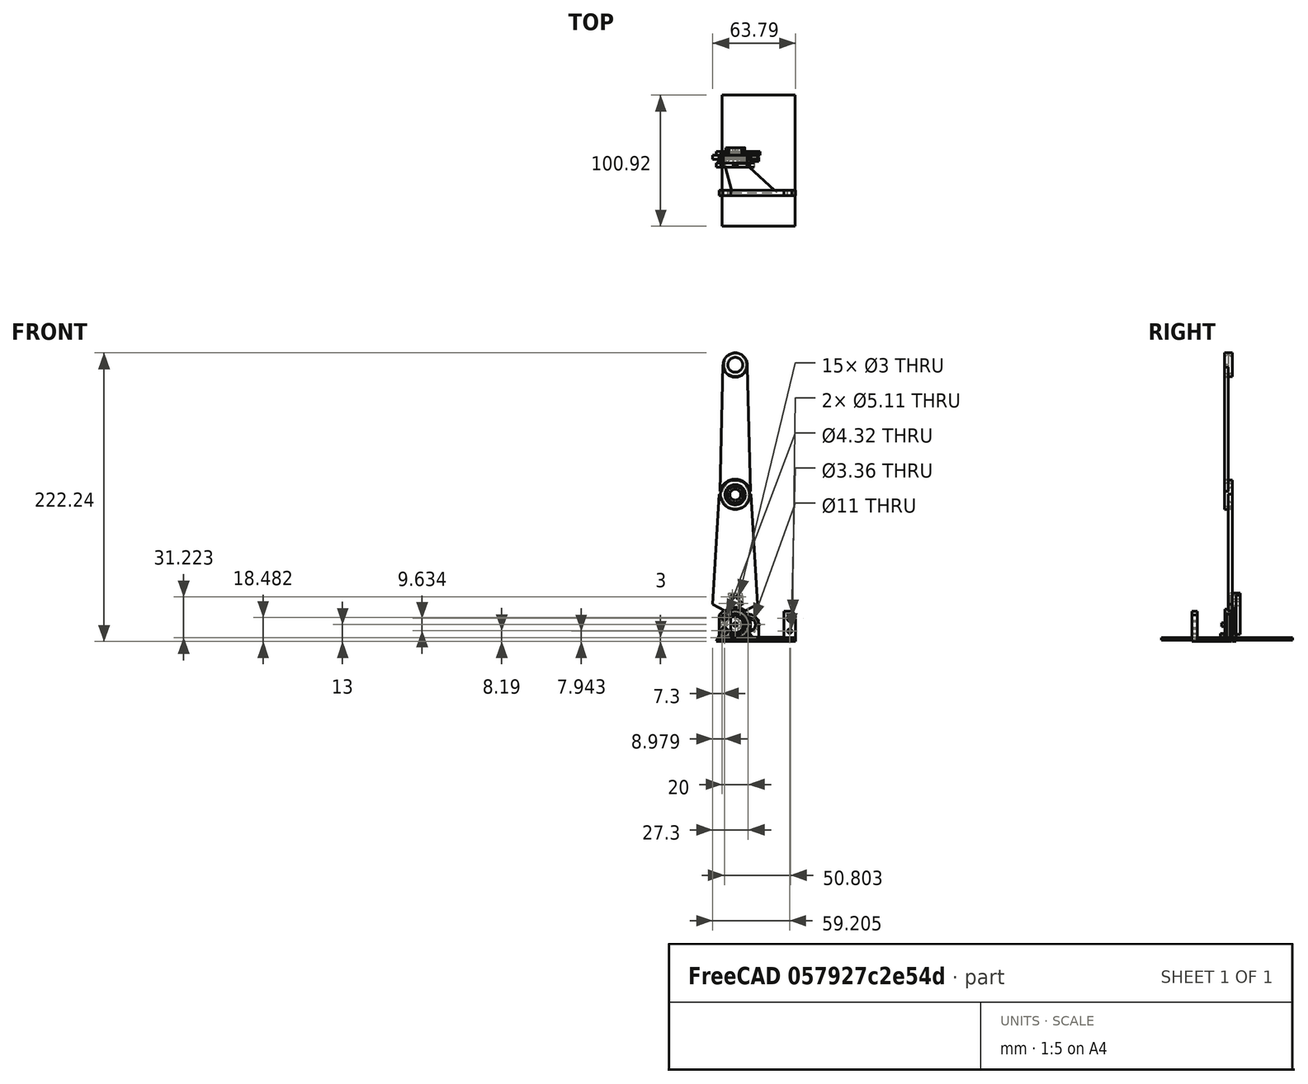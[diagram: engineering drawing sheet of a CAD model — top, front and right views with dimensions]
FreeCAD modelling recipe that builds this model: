
FCSTD DOCUMENT  (FreeCAD 0.16RUnknown)
Label: Arm
License: CreativeCommons Attribution-NonCommercial
LicenseURL: http://creativecommons.org/licenses/by-nc/4.0/
objects: Sketcher::SketchObject×25, PartDesign::Pad×12, PartDesign::Revolution×6, Mesh::Feature×3, Part::Cut×3, Part::Cylinder×2, Part::MultiFuse×2, Part::FeaturePython×2
note: 70 computed .brp shape members not serialized (recipe doc carries the construction recipe); baked Part::Feature solids carry a one-line shape summary decoded from their .brp

FEATURE [Mesh::Feature] ParallaxServo
  Placement = pos=(2,50,0) rot=(1,0,0;1.5708rad)
FEATURE [Sketcher::SketchObject] Sketch
  sketch-geometry (1):
    g0: Circle CenterX=0 CenterY=0 CenterZ=0 NormalX=0 NormalY=0 NormalZ=1 Radius=85.2865
  constraints (1):
    c: Coincident(g0,g-1)
FEATURE [Mesh::Feature] ParallaxServo001
  Placement = pos=(15,-50,0) rot=(0.57735,-0.57735,-0.57735;4.18879rad)
FEATURE [Sketcher::SketchObject] Sketch001
  Placement = pos=(10,0,0) rot=(1,0,0;1.5708rad)
  sketch-geometry (6):
    g0: Circle CenterX=0 CenterY=0 CenterZ=0 NormalX=0 NormalY=0 NormalZ=1 Radius=5.5
    g1: ArcOfCircle CenterX=0 CenterY=0 CenterZ=0 NormalX=0 NormalY=0 NormalZ=1 Radius=8 StartAngle=0 EndAngle=3.14159
    g2: LineSegment StartX=-8 StartY=0 StartZ=0 EndX=-8 EndY=-10 EndZ=0
    g3: LineSegment StartX=-8 StartY=-10 StartZ=0 EndX=8 EndY=-10 EndZ=0
    g4: LineSegment StartX=8 StartY=-10 StartZ=0 EndX=8 EndY=0 EndZ=0
    g5: LineSegment [constr] StartX=-8 StartY=0 StartZ=0 EndX=-5.5 EndY=0 EndZ=0
  constraints (17):
    c: PointOnObject(g0,g-1)
    c: Coincident(g0,g-1)
    c: Radius(g0) = 5.5
    c: Coincident(g1,g-1)
    c: PointOnObject(g1,g-1)
    c: PointOnObject(g1,g-1)
    c: Tangent(g1,g2) = -1.5708
    c: Coincident(g2,g3)
    c: Horizontal(g3)
    c: Coincident(g3,g4)
    c: Coincident(g4,g1)
    c: Vertical(g4)
    c: DistanceY(g2,g-1) = 10
    c: Coincident(g5,g1)
    c: PointOnObject(g5,g0)
    c: Horizontal(g5)
    c: DistanceX(g5,g5) = 2.5
FEATURE [Sketcher::SketchObject] Sketch002
  Placement = pos=(0,0,-10) rot=(0,0,1;0rad)
  sketch-geometry (4):
    g0: LineSegment StartX=-10.0536 StartY=49.3948 StartZ=0 EndX=45.9875 EndY=49.3948 EndZ=0
    g1: LineSegment StartX=45.9875 StartY=49.3948 StartZ=0 EndX=45.9875 EndY=-51.5305 EndZ=0
    g2: LineSegment StartX=45.9875 StartY=-51.5305 StartZ=0 EndX=-10.0536 EndY=-51.5305 EndZ=0
    g3: LineSegment StartX=-10.0536 StartY=-51.5305 StartZ=0 EndX=-10.0536 EndY=49.3948 EndZ=0
  constraints (8):
    c: Coincident(g0,g1)
    c: Coincident(g1,g2)
    c: Coincident(g2,g3)
    c: Coincident(g3,g0)
    c: Horizontal(g0)
    c: Horizontal(g2)
    c: Vertical(g1)
    c: Vertical(g3)
FEATURE [PartDesign::Pad] Pad
  Length = 2
  Length2 = 100
  Placement = pos=(0,0,-10) rot=(0,0,1;0rad)
  Reversed = true
  Sketch = -> Sketch002
  Type = 0
FEATURE [PartDesign::Pad] Pad001
  Length = 3
  Length2 = 100
  Midplane = true
  Placement = pos=(10,0,0) rot=(1,0,0;1.5708rad)
  Sketch = -> Sketch001
  Type = 0
FEATURE [Sketcher::SketchObject] Sketch003
  Placement = pos=(0,0,0) rot=(-1,0,0;4.71239rad)
FEATURE [Sketcher::SketchObject] Sketch004
  Placement = pos=(0,0,0) rot=(0.57735,0.57735,0.57735;2.0944rad)
  sketch-geometry (13):
    g0: LineSegment [constr] StartX=-2.5 StartY=6.31119 StartZ=0 EndX=0 EndY=4.21345 EndZ=0
    g1: LineSegment StartX=0 StartY=4.21345 StartZ=0 EndX=2.5 EndY=6.31119 EndZ=0
    g2: LineSegment StartX=2.5 StartY=6.31119 StartZ=0 EndX=2.5 EndY=0 EndZ=0
    g3: LineSegment [constr] StartX=-2.5 StartY=0 StartZ=0 EndX=-2.5 EndY=6.31119 EndZ=0
    g4: LineSegment [constr] StartX=-2.5 StartY=6.31119 StartZ=0 EndX=2.5 EndY=6.31119 EndZ=0
    g5: Circle [constr] CenterX=0 CenterY=7.28115 CenterZ=0 NormalX=0 NormalY=0 NormalZ=1 Radius=2.35
    g6: LineSegment [constr] StartX=-2.5 StartY=0 StartZ=0 EndX=2.5 EndY=0 EndZ=0
    g7: Circle [constr] CenterX=-4.27975 CenterY=5.89058 CenterZ=0 NormalX=0 NormalY=0 NormalZ=1 Radius=2.25
    g8: Circle [constr] CenterX=0 CenterY=7.28115 CenterZ=0 NormalX=0 NormalY=0 NormalZ=1 Radius=2.25
    g9: ArcOfCircle [constr] CenterX=0 CenterY=0 CenterZ=0 NormalX=0 NormalY=0 NormalZ=1 Radius=7.28115 StartAngle=1.5708 EndAngle=2.19911
    g10: LineSegment [constr] StartX=-4.27975 StartY=5.89058 StartZ=0 EndX=0 EndY=0 EndZ=0
    g11: LineSegment StartX=0 StartY=4.21345 StartZ=0 EndX=0 EndY=0 EndZ=0
    g12: LineSegment StartX=0 StartY=0 StartZ=0 EndX=2.5 EndY=0 EndZ=0
  constraints (33):
    c: PointOnObject(g0,g-2)
    c: Coincident(g0,g1)
    c: Coincident(g1,g2)
    c: Coincident(g3,g0)
    c: Vertical(g3)
    c: Coincident(g4,g0)
    c: Coincident(g4,g1)
    c: Horizontal(g4)
    c: PointOnObject(g5,g-2)
    c: Tangent(g1,g5)
    c: Radius(g5) = 2.35
    c: Tangent(g5,g0)
    c: Angle(g1,g0) = 1.74533
    c: DistanceX(g4,g4) = 5
    c: Vertical(g2)
    c: Coincident(g6,g3)
    c: Coincident(g6,g2)
    c: PointOnObject(g3,g-1)
    c: PointOnObject(g2,g-1)
    c: Coincident(g8,g5)
    c: Radius(g8) = 2.25
    c: Equal(g8,g7)
    c: Tangent(g7,g8)
    c: Coincident(g9,g-1)
    c: Coincident(g9,g5)
    c: Coincident(g9,g7)
    c: Coincident(g10,g7)
    c: Coincident(g10,g-1)
    c: Angle(g-2,g10) = 0.628319
    c: Coincident(g0,g11)
    c: Coincident(g11,g12)
    c: Coincident(g12,g2)
    c: Coincident(g11,g-1)
FEATURE [PartDesign::Revolution] Revolution
  Angle = 360
  Axis = (0,1,0)
  Base = (0,0,0)
  Placement = pos=(0,0,0) rot=(0.57735,0.57735,0.57735;2.0944rad)
  ReferenceAxis = -> Sketch004 [H_Axis]
  Sketch = -> Sketch004
FEATURE [Sketcher::SketchObject] Sketch006
  Placement = pos=(0,0,0) rot=(1,0,0;1.5708rad)
  sketch-geometry (4):
    g0: Circle [constr] CenterX=0 CenterY=0 CenterZ=0 NormalX=0 NormalY=0 NormalZ=1 Radius=7.28115
    g1: Circle CenterX=7.28115 CenterY=0 CenterZ=0 NormalX=0 NormalY=0 NormalZ=1 Radius=2.25
    g2: Circle CenterX=5.89058 CenterY=4.27975 CenterZ=0 NormalX=0 NormalY=0 NormalZ=1 Radius=2.25
    g3: LineSegment [constr] StartX=5.89058 StartY=4.27975 StartZ=0 EndX=0 EndY=0 EndZ=0
  constraints (11):
    c: Coincident(g0,g-1)
    c: PointOnObject(g1,g0)
    c: PointOnObject(g2,g0)
    c: Equal(g2,g1)
    c: Coincident(g3,g2)
    c: Coincident(g3,g-1)
    c: Angle(g-1,g3) = 0.628319
    c: Tangent(g2,g1)
    c: Radius(g1) = 2.25
    c: PointOnObject(g1,g-1)
    c: Distance(g3) = 7.28115
FEATURE [Sketcher::SketchObject] Sketch007
  Placement = pos=(0,0,0) rot=(0.57735,0.57735,0.57735;2.0944rad)
  sketch-geometry (10):
    g0: Circle [constr] CenterX=0 CenterY=7.28115 CenterZ=0 NormalX=0 NormalY=0 NormalZ=1 Radius=2.35
    g1: Circle [constr] CenterX=-4.27975 CenterY=5.89058 CenterZ=0 NormalX=0 NormalY=0 NormalZ=1 Radius=2.25
    g2: Circle [constr] CenterX=0 CenterY=7.28115 CenterZ=0 NormalX=0 NormalY=0 NormalZ=1 Radius=2.25
    g3: ArcOfCircle [constr] CenterX=0 CenterY=0 CenterZ=0 NormalX=0 NormalY=0 NormalZ=1 Radius=7.28115 StartAngle=1.5708 EndAngle=2.19911
    g4: LineSegment [constr] StartX=-4.27975 StartY=5.89058 StartZ=0 EndX=0 EndY=0 EndZ=0
    g5: LineSegment StartX=-2.5 StartY=8.25111 StartZ=0 EndX=0 EndY=10.3489 EndZ=0
    g6: LineSegment StartX=0 StartY=10.3489 StartZ=0 EndX=2.5 EndY=8.25111 EndZ=0
    g7: LineSegment StartX=2.5 StartY=8.25111 StartZ=0 EndX=2.5 EndY=11.7511 EndZ=0
    g8: LineSegment StartX=2.5 StartY=11.7511 StartZ=0 EndX=-2.5 EndY=11.7511 EndZ=0
    g9: LineSegment StartX=-2.5 StartY=11.7511 StartZ=0 EndX=-2.5 EndY=8.25111 EndZ=0
  constraints (26):
    c: PointOnObject(g0,g-2)
    c: Radius(g0) = 2.35
    c: Coincident(g2,g0)
    c: Radius(g2) = 2.25
    c: Equal(g2,g1)
    c: Tangent(g1,g2)
    c: Coincident(g3,g-1)
    c: Coincident(g3,g0)
    c: Coincident(g3,g1)
    c: Coincident(g4,g1)
    c: Coincident(g4,g-1)
    c: Angle(g-2,g4) = 0.628319
    c: Coincident(g5,g6)
    c: Coincident(g6,g7)
    c: Coincident(g7,g8)
    c: Horizontal(g8)
    c: Coincident(g8,g9)
    c: Coincident(g5,g9)
    c: Vertical(g7)
    c: Vertical(g9)
    c: Symmetric(g5,g6,g-2)
    c: Tangent(g5,g0)
    c: Tangent(g6,g0)
    c: DistanceX(g8,g8) = 5
    c: Angle(g5,g6) = 1.74533
    c: DistanceY(g7,g7) = 3.5
FEATURE [PartDesign::Revolution] Revolution001  label="OuterBearing"
  Angle = 360
  Axis = (0,1,0)
  Base = (0,0,0)
  Placement = pos=(0,0,0) rot=(0.57735,0.57735,0.57735;2.0944rad)
  ReferenceAxis = -> Sketch007 [H_Axis]
  Sketch = -> Sketch007
FEATURE [Part::Cylinder] Cylinder
  Angle = 360
  Height = 10
  Placement = pos=(0,5,0) rot=(1,0,0;1.5708rad)
  Radius = 1.5
FEATURE [Part::Cut] Cut  label="InnerBearing"
  Base = -> Revolution
  Placement = pos=(0,0,0) rot=(0,0,1;3.14159rad)
  Tool = -> Cylinder
FEATURE [Sketcher::SketchObject] Sketch008
  Placement = pos=(0,0,0) rot=(0.57735,0.57735,0.57735;2.0944rad)
  sketch-geometry (14):
    g0: LineSegment [constr] StartX=-2.5 StartY=6.31119 StartZ=0 EndX=0 EndY=4.21345 EndZ=0
    g1: LineSegment StartX=0 StartY=4.21345 StartZ=0 EndX=2.5 EndY=6.31119 EndZ=0
    g2: LineSegment [constr] StartX=-2.5 StartY=0 StartZ=0 EndX=-2.5 EndY=6.31119 EndZ=0
    g3: LineSegment [constr] StartX=-2.5 StartY=6.31119 StartZ=0 EndX=2.5 EndY=6.31119 EndZ=0
    g4: Circle [constr] CenterX=0 CenterY=7.28115 CenterZ=0 NormalX=0 NormalY=0 NormalZ=1 Radius=2.35
    g5: LineSegment [constr] StartX=-2.5 StartY=0 StartZ=0 EndX=3.25 EndY=0 EndZ=0
    g6: Circle [constr] CenterX=-4.27975 CenterY=5.89058 CenterZ=0 NormalX=0 NormalY=0 NormalZ=1 Radius=2.25
    g7: Circle [constr] CenterX=0 CenterY=7.28115 CenterZ=0 NormalX=0 NormalY=0 NormalZ=1 Radius=2.25
    g8: ArcOfCircle [constr] CenterX=0 CenterY=0 CenterZ=0 NormalX=0 NormalY=0 NormalZ=1 Radius=7.28115 StartAngle=1.5708 EndAngle=2.19911
    g9: LineSegment [constr] StartX=-4.27975 StartY=5.89058 StartZ=0 EndX=0 EndY=0 EndZ=0
    g10: LineSegment StartX=0 StartY=4.21345 StartZ=0 EndX=0 EndY=0 EndZ=0
    g11: LineSegment StartX=0 StartY=0 StartZ=0 EndX=3.25 EndY=0 EndZ=0
    g12: LineSegment StartX=2.5 StartY=6.31119 StartZ=0 EndX=3.25 EndY=6.31119 EndZ=0
    g13: LineSegment StartX=3.25 StartY=6.31119 StartZ=0 EndX=3.25 EndY=0 EndZ=0
  constraints (36):
    c: PointOnObject(g0,g-2)
    c: Coincident(g0,g1)
    c: Coincident(g2,g0)
    c: Vertical(g2)
    c: Coincident(g3,g0)
    c: Coincident(g3,g1)
    c: Horizontal(g3)
    c: PointOnObject(g4,g-2)
    c: Tangent(g1,g4)
    c: Radius(g4) = 2.35
    c: Tangent(g4,g0)
    c: Angle(g1,g0) = 1.74533
    c: DistanceX(g3,g3) = 5
    c: Coincident(g5,g2)
    c: PointOnObject(g2,g-1)
    c: PointOnObject(g5,g-1)
    c: Coincident(g7,g4)
    c: Radius(g7) = 2.25
    c: Equal(g7,g6)
    c: Tangent(g6,g7)
    c: Coincident(g8,g-1)
    c: Coincident(g8,g4)
    c: Coincident(g8,g6)
    c: Coincident(g9,g6)
    c: Coincident(g9,g-1)
    c: Angle(g-2,g9) = 0.628319
    c: Coincident(g0,g10)
    c: Coincident(g10,g11)
    c: Coincident(g10,g-1)
    c: Coincident(g1,g12)
    c: Horizontal(g12)
    c: Coincident(g12,g13)
    c: Coincident(g13,g5)
    c: Vertical(g13)
    c: DistanceX(g12,g12) = 0.75
    c: Coincident(g11,g5)
FEATURE [Part::Cylinder] Cylinder001
  Angle = 360
  Height = 10
  Placement = pos=(0,5,0) rot=(1,0,0;1.5708rad)
  Radius = 1.5
FEATURE [PartDesign::Revolution] Revolution002  label="InnerBearing001"
  Angle = 360
  Axis = (0,1,0)
  Base = (0,0,0)
  Placement = pos=(0,0,0) rot=(0.57735,0.57735,0.57735;2.0944rad)
  ReferenceAxis = -> Sketch008 [H_Axis]
  Sketch = -> Sketch008
FEATURE [Sketcher::SketchObject] Sketch009
  Placement = pos=(0,0,0) rot=(1,0,0;1.5708rad)
  sketch-geometry (7):
    g0: ArcOfCircle CenterX=0 CenterY=0 CenterZ=0 NormalX=0 NormalY=0 NormalZ=1 Radius=13.0115 StartAngle=0.931608 EndAngle=2.20998
    g1: LineSegment StartX=7.76195 StartY=10.4428 StartZ=0 EndX=17.2974 EndY=15.5976 EndZ=0
    g2: LineSegment StartX=17.2974 StartY=15.5976 StartZ=0 EndX=12.2204 EndY=100.443 EndZ=0
    g3: LineSegment StartX=-12.2204 StartY=100.443 StartZ=0 EndX=-17.2974 EndY=15.5976 EndZ=0
    g4: LineSegment StartX=-17.2974 StartY=15.5976 StartZ=0 EndX=-7.76195 EndY=10.4428 EndZ=0
    g5: LineSegment [constr] StartX=56.9262 StartY=123.358 StartZ=0 EndX=56.9262 EndY=23.3583 EndZ=0
    g6: ArcOfCircle CenterX=0 CenterY=102.118 CenterZ=0 NormalX=0 NormalY=0 NormalZ=1 Radius=12.3347 StartAngle=3.27785 EndAngle=6.14693
  constraints (14):
    c: Coincident(g0,g-1)
    c: Symmetric(g3,g2,g-2)
    c: Symmetric(g0,g0,g-2)
    c: Coincident(g0,g1)
    c: Coincident(g1,g2)
    c: Coincident(g3,g4)
    c: Coincident(g4,g0)
    c: Symmetric(g3,g1,g-2)
    c: Vertical(g5)
    c: DistanceY(g5,g5) = 100
    c: DistanceY(g0,g3) = 90
    c: PointOnObject(g6,g-2)
    c: Coincident(g6,g3)
    c: PointOnObject(g6,g2)
FEATURE [PartDesign::Pad] Pad002  label="ArmBase"
  Length = 3
  Length2 = 100
  Placement = pos=(0,0,0) rot=(1,0,0;1.5708rad)
  Reversed = true
  Sketch = -> Sketch009
  Type = 0
FEATURE [Sketcher::SketchObject] Sketch010
  Placement = pos=(0,6,0) rot=(1,0,0;1.5708rad)
  sketch-geometry (4):
    g0: ArcOfCircle CenterX=0 CenterY=0 CenterZ=0 NormalX=0 NormalY=0 NormalZ=1 Radius=7.43127 StartAngle=3.04464 EndAngle=6.38014
    g1: LineSegment StartX=-7.39637 StartY=0.719373 StartZ=0 EndX=-5.27279 EndY=22.5534 EndZ=0
    g2: LineSegment StartX=-5.27279 StartY=22.5534 StartZ=0 EndX=5.27279 EndY=22.5534 EndZ=0
    g3: LineSegment StartX=5.27279 StartY=22.5534 StartZ=0 EndX=7.39637 EndY=0.719373 EndZ=0
  constraints (7):
    c: Coincident(g0,g-1)
    c: Tangent(g0,g1) = 1.5708
    c: Coincident(g1,g2)
    c: Coincident(g2,g3)
    c: Coincident(g3,g0)
    c: Tangent(g3,g0)
    c: Symmetric(g2,g1,g-2)
FEATURE [PartDesign::Pad] Pad003  label="ArmMountBase"
  Length = 3
  Length2 = 100
  Placement = pos=(0,6,0) rot=(1,0,0;1.5708rad)
  Reversed = true
  Sketch = -> Sketch010
  Type = 0
FEATURE [Sketcher::SketchObject] Sketch011
  Placement = pos=(0,0,0) rot=(1,0,0;1.5708rad)
  sketch-geometry (4):
    g0: Circle CenterX=-2.25 CenterY=21.223 CenterZ=0 NormalX=0 NormalY=0 NormalZ=1 Radius=1.5
    g1: Circle CenterX=-3.75 CenterY=16.223 CenterZ=0 NormalX=0 NormalY=0 NormalZ=1 Radius=1.5
    g2: Circle CenterX=2.25 CenterY=21.223 CenterZ=0 NormalX=0 NormalY=0 NormalZ=1 Radius=1.5
    g3: Circle CenterX=3.75 CenterY=16.223 CenterZ=0 NormalX=0 NormalY=0 NormalZ=1 Radius=1.5
  constraints (9):
    c: Radius(g3) = 1.5
    c: Equal(g3,g2)
    c: Equal(g3,g0)
    c: Equal(g3,g1)
    c: Symmetric(g0,g2,g-2)
    c: Symmetric(g3,g1,g-2)
    c: DistanceX(g1,g3) = 7.5
    c: DistanceX(g0,g2) = 4.5
    c: DistanceY(g3,g2) = 5
FEATURE [PartDesign::Pad] Pad004  label="ArmMountCutout"
  Length = 20
  Length2 = 100
  Midplane = true
  Placement = pos=(0,0,0) rot=(1,0,0;1.5708rad)
  Sketch = -> Sketch011
  Type = 0
FEATURE [Sketcher::SketchObject] Sketch012
  Placement = pos=(0,9,0) rot=(1,0,0;1.5708rad)
  sketch-geometry (4):
    g0: ArcOfCircle CenterX=0 CenterY=0 CenterZ=0 NormalX=0 NormalY=0 NormalZ=1 Radius=13.8052 StartAngle=1.1061 EndAngle=2.03549
    g1: LineSegment StartX=-6.18676 StartY=12.3413 StartZ=0 EndX=-5.02905 EndY=24.2455 EndZ=0
    g2: LineSegment StartX=-5.02905 StartY=24.2455 StartZ=0 EndX=5.02905 EndY=24.2455 EndZ=0
    g3: LineSegment StartX=5.02905 StartY=24.2455 StartZ=0 EndX=6.18676 EndY=12.3413 EndZ=0
  constraints (8):
    c: Coincident(g0,g-1)
    c: Coincident(g0,g1)
    c: Coincident(g1,g2)
    c: Horizontal(g2)
    c: Coincident(g2,g3)
    c: Coincident(g3,g0)
    c: Symmetric(g0,g0,g-2)
    c: Symmetric(g2,g1,g-2)
FEATURE [PartDesign::Pad] Pad005  label="ArmMountPad"
  Length = 7.5
  Length2 = 100
  Placement = pos=(0,9,0) rot=(1,0,0;1.5708rad)
  Sketch = -> Sketch012
  Type = 0
FEATURE [Part::MultiFuse] Fusion
  Shapes = -> [Revolution002,Pad005,Pad003]
FEATURE [Part::Cut] Cut001
  Base = -> Fusion
  Tool = -> Pad004
FEATURE [Part::Cut] Cut002
  Base = -> Pad002
  Tool = -> Pad004
FEATURE [Sketcher::SketchObject] Sketch013
  Placement = pos=(0,0,-10) rot=(0,0,1;0rad)
  Support = -> Pad [Face5]
FEATURE [Sketcher::SketchObject] Sketch014
  Placement = pos=(0,0,0) rot=(1,0,0;1.5708rad)
  sketch-geometry (6):
    g0: ArcOfCircle CenterX=0 CenterY=0 CenterZ=0 NormalX=0 NormalY=0 NormalZ=1 Radius=11.5 StartAngle=3.59139 EndAngle=4.71239
    g1: LineSegment StartX=-10.3562 StartY=-5 StartZ=0 EndX=-12.3562 EndY=-5 EndZ=0
    g2: LineSegment StartX=-12.3562 StartY=-5 StartZ=0 EndX=-15.0859 EndY=-12.5 EndZ=0
    g3: LineSegment StartX=-15.0859 StartY=-12.5 StartZ=0 EndX=0 EndY=-12.5 EndZ=0
    g4: LineSegment StartX=0 StartY=-11.5 StartZ=0 EndX=0 EndY=-12.5 EndZ=0
    g5: Circle CenterX=-10 CenterY=-9.5 CenterZ=0 NormalX=0 NormalY=0 NormalZ=1 Radius=1.5
  constraints (18):
    c: Coincident(g0,g-1)
    c: Coincident(g1,g0)
    c: Horizontal(g1)
    c: Coincident(g1,g2)
    c: Coincident(g2,g3)
    c: Horizontal(g3)
    c: Radius(g0) = 11.5
    c: DistanceY(g0,g-1) = 5
    c: PointOnObject(g0,g-2)
    c: Coincident(g4,g0)
    c: Coincident(g4,g3)
    c: Vertical(g4)
    c: DistanceY(g4,g4) = 1
    c: DistanceX(g1,g1) = 2
    c: Angle(g3,g2) = 1.22173
    c: Radius(g5) = 1.5
    c: DistanceX(g5,g-1) = 10
    c: DistanceY(g3,g5) = 3
FEATURE [Sketcher::SketchObject] Sketch015
FEATURE [Sketcher::SketchObject] Sketch016
  Placement = pos=(0,3,0) rot=(1,0,0;1.5708rad)
  sketch-geometry (8):
    g0: ArcOfCircle CenterX=0 CenterY=0 CenterZ=0 NormalX=0 NormalY=0 NormalZ=1 Radius=11.5 StartAngle=3.79601 EndAngle=5.62877
    g1: Circle CenterX=-10 CenterY=-10 CenterZ=0 NormalX=0 NormalY=0 NormalZ=1 Radius=1.5
    g2: Circle CenterX=10 CenterY=-10 CenterZ=0 NormalX=0 NormalY=0 NormalZ=1 Radius=1.5
    g3: LineSegment StartX=-14.5882 StartY=-13 StartZ=0 EndX=14.5882 EndY=-13 EndZ=0
    g4: LineSegment StartX=14.5882 StartY=-13 StartZ=0 EndX=11.1241 EndY=-7 EndZ=0
    g5: LineSegment StartX=11.1241 StartY=-7 StartZ=0 EndX=9.12414 EndY=-7 EndZ=0
    g6: LineSegment StartX=-9.12414 StartY=-7 StartZ=0 EndX=-11.1241 EndY=-7 EndZ=0
    g7: LineSegment StartX=-11.1241 StartY=-7 StartZ=0 EndX=-14.5882 EndY=-13 EndZ=0
  constraints (22):
    c: Coincident(g0,g-1)
    c: Radius(g2) = 1.5
    c: Equal(g2,g1)
    c: Symmetric(g1,g2,g-2)
    c: DistanceX(g1,g2) = 20
    c: Horizontal(g3)
    c: Coincident(g3,g4)
    c: Coincident(g4,g5)
    c: Coincident(g5,g0)
    c: Coincident(g6,g7)
    c: Coincident(g7,g3)
    c: DistanceY(g3,g1) = 3
    c: DistanceY(g3,g-1) = 13
    c: Angle(g3,g7) = 1.0472
    c: Horizontal(g6)
    c: Symmetric(g6,g4,g-2)
    c: Symmetric(g3,g3,g-2)
    c: Coincident(g6,g0)
    c: Symmetric(g0,g0,g-2)
    c: DistanceX(g6,g6) = 2
    c: Radius(g0) = 11.5
    c: DistanceY(g3,g6) = 6
FEATURE [PartDesign::Pad] Pad007
  Length = 3
  Length2 = 100
  Placement = pos=(0,3,0) rot=(1,0,0;1.5708rad)
  Reversed = true
  Sketch = -> Sketch016
  Type = 0
FEATURE [Mesh::Feature] ParallaxServo002
  Placement = pos=(15,-50,0) rot=(-1,0,0;1.5708rad)
FEATURE [Sketcher::SketchObject] Sketch017
  Placement = pos=(0,0,0) rot=(1,0,0;1.5708rad)
  sketch-geometry (8):
    g0: ArcOfCircle CenterX=0 CenterY=0 CenterZ=0 NormalX=0 NormalY=0 NormalZ=1 Radius=11.5 StartAngle=3.68542 EndAngle=5.73935
    g1: Circle CenterX=10 CenterY=-10 CenterZ=0 NormalX=0 NormalY=0 NormalZ=1 Radius=1.5
    g2: ArcOfCircle CenterX=-10 CenterY=-10 CenterZ=0 NormalX=0 NormalY=0 NormalZ=1 Radius=3 StartAngle=2.26893 EndAngle=4.71239
    g3: ArcOfCircle CenterX=10 CenterY=-10 CenterZ=0 NormalX=0 NormalY=0 NormalZ=1 Radius=3 StartAngle=4.71239 EndAngle=7.15585
    g4: LineSegment StartX=-10 StartY=-13 StartZ=0 EndX=10 EndY=-13 EndZ=0
    g5: LineSegment StartX=-9.84093 StartY=-5.9503 StartZ=0 EndX=-11.9284 EndY=-7.70187 EndZ=0
    g6: LineSegment StartX=11.9284 StartY=-7.70186 StartZ=0 EndX=9.84093 EndY=-5.9503 EndZ=0
    g7: Circle CenterX=-10 CenterY=-10 CenterZ=0 NormalX=0 NormalY=0 NormalZ=1 Radius=1.5
  constraints (23):
    c: Coincident(g0,g-1)
    c: Radius(g1) = 1.5
    c: Symmetric(g0,g0,g-2)
    c: Radius(g0) = 11.5
    c: Coincident(g4,g2)
    c: Coincident(g4,g3)
    c: Horizontal(g4)
    c: Tangent(g2,g4)
    c: Tangent(g4,g3)
    c: DistanceY(g3,g-1) = 13
    c: Radius(g2) = 3
    c: Coincident(g5,g0)
    c: Coincident(g5,g2)
    c: Coincident(g6,g3)
    c: Coincident(g6,g0)
    c: Coincident(g3,g1)
    c: Coincident(g7,g2)
    c: Equal(g7,g1)
    c: Symmetric(g2,g1,g-2)
    c: Tangent(g6,g3)
    c: Tangent(g5,g2)
    c: Distance(g1,g2) = 20
    c: Angle(g6,g4) = 0.698132
FEATURE [PartDesign::Pad] Pad008  label="BearingMount"
  Length = 5
  Length2 = 100
  Midplane = true
  Placement = pos=(0,0,0) rot=(1,0,0;1.5708rad)
  Sketch = -> Sketch017
  Type = 0
FEATURE [Part::MultiFuse] Fusion001
  Shapes = -> [Pad008,Revolution001]
FEATURE [Part::FeaturePython] InvoluteGear  # WARN: FeaturePython — macro-defined, semantics opaque (R4)
  Placement = pos=(0,6,0) rot=(1,0,0;1.5708rad)
  backlash = 0
  beta = 0
  clearance = 0.25
  height = 3
  module = 1
  numpoints = 6
  pressure_angle = 20
  shift = 0
  simple = false
  teeth = 20
  undercut = false
FEATURE [Part::FeaturePython] InvoluteGear001  # WARN: FeaturePython — macro-defined, semantics opaque (R4)
  Placement = pos=(13,6,0) rot=(1,0,0;1.5708rad)
  backlash = 0
  beta = 0
  clearance = 0.25
  height = 3
  module = 1
  numpoints = 6
  pressure_angle = 20
  shift = 0
  simple = false
  teeth = 10
  undercut = false
FEATURE [Sketcher::SketchObject] Sketch018
  Placement = pos=(2,-24,0) rot=(1,0,0;1.5708rad)
  sketch-geometry (14):
    g0: LineSegment StartX=-5.45651 StartY=10.1523 StartZ=0 EndX=-11.4898 EndY=10.1523 EndZ=0
    g1: LineSegment StartX=-11.4898 StartY=10.1523 StartZ=0 EndX=-14.4067 EndY=7.23543 EndZ=0
    g2: LineSegment StartX=-14.4067 StartY=7.23543 StartZ=0 EndX=-14.4067 EndY=-13 EndZ=0
    g3: LineSegment StartX=-14.4067 StartY=-13 StartZ=0 EndX=44.4937 EndY=-13 EndZ=0
    g4: LineSegment StartX=44.4937 StartY=-13 StartZ=0 EndX=44.4937 EndY=7.23543 EndZ=0
    g5: LineSegment StartX=44.4937 StartY=7.23543 StartZ=0 EndX=41.5768 EndY=10.1523 EndZ=0
    g6: LineSegment StartX=41.5768 StartY=10.1523 StartZ=0 EndX=35.5435 EndY=10.1523 EndZ=0
    g7: LineSegment StartX=35.5435 StartY=10.1523 StartZ=0 EndX=35.5435 EndY=-9.84766 EndZ=0
    g8: LineSegment StartX=35.5435 StartY=-9.84766 StartZ=0 EndX=-5.45651 EndY=-9.84766 EndZ=0
    g9: LineSegment StartX=-5.45651 StartY=-9.84766 StartZ=0 EndX=-5.45651 EndY=10.1523 EndZ=0
    g10: Circle CenterX=-10.3208 CenterY=5.48196 CenterZ=0 NormalX=0 NormalY=0 NormalZ=1 Radius=2.16127
    g11: Circle CenterX=-10.3208 CenterY=-4.81028 CenterZ=0 NormalX=0 NormalY=0 NormalZ=1 Radius=2.55646
    g12: Circle CenterX=40.4818 CenterY=4.82326 CenterZ=0 NormalX=0 NormalY=0 NormalZ=1 Radius=2.5538
    g13: Circle CenterX=39.9054 CenterY=-5.05729 CenterZ=0 NormalX=0 NormalY=0 NormalZ=1 Radius=1.67937
  constraints (26):
    c: Horizontal(g0)
    c: Coincident(g0,g1)
    c: Coincident(g1,g2)
    c: Vertical(g2)
    c: Coincident(g2,g3)
    c: Horizontal(g3)
    c: Coincident(g3,g4)
    c: Vertical(g4)
    c: Coincident(g4,g5)
    c: Coincident(g5,g6)
    c: Horizontal(g6)
    c: Coincident(g6,g7)
    c: Vertical(g7)
    c: Coincident(g7,g8)
    c: Horizontal(g8)
    c: Coincident(g8,g9)
    c: Coincident(g9,g0)
    c: Vertical(g9)
    c: Equal(g7,g9)
    c: DistanceX(g8,g8) = 41
    c: DistanceY(g9,g9) = 20
    c: DistanceY(g2,g-1) = 13
    c: Angle(g1,g0) = 2.35619
    c: Equal(g6,g0)
    c: Angle(g6,g5) = 2.35619
    c: Equal(g1,g5)
FEATURE [PartDesign::Pad] Pad009
  Length = 4
  Length2 = 100
  Placement = pos=(2,-24,0) rot=(1,0,0;1.5708rad)
  Sketch = -> Sketch018
  Type = 0
FEATURE [Sketcher::SketchObject] Sketch019
  Placement = pos=(0,0,-13) rot=(0,0,1;0rad)
  sketch-geometry (4):
    g0: LineSegment StartX=-8.28506 StartY=-3.06297 StartZ=0 EndX=-2.33384 EndY=-25.6108 EndZ=0
    g1: LineSegment StartX=-2.33384 StartY=-25.6108 StartZ=0 EndX=31.9368 EndY=-25.6108 EndZ=0
    g2: LineSegment StartX=31.9368 StartY=-25.6108 StartZ=0 EndX=7.92901 EndY=-3.18581 EndZ=0
    g3: LineSegment StartX=7.92901 StartY=-3.18581 StartZ=0 EndX=-8.28506 EndY=-3.06297 EndZ=0
  constraints (5):
    c: Coincident(g0,g1)
    c: Horizontal(g1)
    c: Coincident(g1,g2)
    c: Coincident(g2,g3)
    c: Coincident(g3,g0)
FEATURE [PartDesign::Pad] Pad010
  Length = 3
  Length2 = 100
  Placement = pos=(0,0,-13) rot=(0,0,1;0rad)
  Sketch = -> Sketch019
  Type = 0
FEATURE [Sketcher::SketchObject] Sketch020
  Placement = pos=(0,-3,0) rot=(1,0,0;1.5708rad)
  sketch-geometry (8):
    g0: ArcOfCircle CenterX=0 CenterY=0 CenterZ=0 NormalX=0 NormalY=0 NormalZ=1 Radius=11.5 StartAngle=3.79601 EndAngle=5.62877
    g1: Circle CenterX=-10 CenterY=-10 CenterZ=0 NormalX=0 NormalY=0 NormalZ=1 Radius=1.5
    g2: Circle CenterX=10 CenterY=-10 CenterZ=0 NormalX=0 NormalY=0 NormalZ=1 Radius=1.5
    g3: LineSegment StartX=-14.5882 StartY=-13 StartZ=0 EndX=14.5882 EndY=-13 EndZ=0
    g4: LineSegment StartX=14.5882 StartY=-13 StartZ=0 EndX=11.1241 EndY=-7 EndZ=0
    g5: LineSegment StartX=11.1241 StartY=-7 StartZ=0 EndX=9.12414 EndY=-7 EndZ=0
    g6: LineSegment StartX=-9.12414 StartY=-7 StartZ=0 EndX=-11.1241 EndY=-7 EndZ=0
    g7: LineSegment StartX=-11.1241 StartY=-7 StartZ=0 EndX=-14.5882 EndY=-13 EndZ=0
  constraints (22):
    c: Coincident(g0,g-1)
    c: Radius(g2) = 1.5
    c: Equal(g2,g1)
    c: Symmetric(g1,g2,g-2)
    c: DistanceX(g1,g2) = 20
    c: Horizontal(g3)
    c: Coincident(g3,g4)
    c: Coincident(g4,g5)
    c: Coincident(g5,g0)
    c: Coincident(g6,g7)
    c: Coincident(g7,g3)
    c: DistanceY(g3,g1) = 3
    c: DistanceY(g3,g-1) = 13
    c: Angle(g3,g7) = 1.0472
    c: Horizontal(g6)
    c: Symmetric(g6,g4,g-2)
    c: Symmetric(g3,g3,g-2)
    c: Coincident(g6,g0)
    c: Symmetric(g0,g0,g-2)
    c: DistanceX(g6,g6) = 2
    c: Radius(g0) = 11.5
    c: DistanceY(g3,g6) = 6
FEATURE [PartDesign::Pad] Pad011
  Length = 3
  Length2 = 100
  Placement = pos=(0,-3,0) rot=(1,0,0;1.5708rad)
  Sketch = -> Sketch020
  Type = 0
FEATURE [Sketcher::SketchObject] Sketch021
  Placement = pos=(0,0,100) rot=(0.57735,0.57735,0.57735;2.0944rad)
  sketch-geometry (10):
    g0: Circle [constr] CenterX=0 CenterY=7.28115 CenterZ=0 NormalX=0 NormalY=0 NormalZ=1 Radius=2.35
    g1: Circle [constr] CenterX=-4.27975 CenterY=5.89058 CenterZ=0 NormalX=0 NormalY=0 NormalZ=1 Radius=2.25
    g2: Circle [constr] CenterX=0 CenterY=7.28115 CenterZ=0 NormalX=0 NormalY=0 NormalZ=1 Radius=2.25
    g3: ArcOfCircle [constr] CenterX=0 CenterY=0 CenterZ=0 NormalX=0 NormalY=0 NormalZ=1 Radius=7.28115 StartAngle=1.5708 EndAngle=2.19911
    g4: LineSegment [constr] StartX=-4.27975 StartY=5.89058 StartZ=0 EndX=0 EndY=0 EndZ=0
    g5: LineSegment StartX=-3 StartY=7.83156 StartZ=0 EndX=0 EndY=10.3489 EndZ=0
    g6: LineSegment StartX=0 StartY=10.3489 StartZ=0 EndX=3 EndY=7.83156 EndZ=0
    g7: LineSegment StartX=3 StartY=7.83156 StartZ=0 EndX=3 EndY=11.3316 EndZ=0
    g8: LineSegment StartX=3 StartY=11.3316 StartZ=0 EndX=-3 EndY=11.3316 EndZ=0
    g9: LineSegment StartX=-3 StartY=11.3316 StartZ=0 EndX=-3 EndY=7.83156 EndZ=0
  constraints (26):
    c: PointOnObject(g0,g-2)
    c: Radius(g0) = 2.35
    c: Coincident(g2,g0)
    c: Radius(g2) = 2.25
    c: Equal(g2,g1)
    c: Tangent(g1,g2)
    c: Coincident(g3,g-1)
    c: Coincident(g3,g0)
    c: Coincident(g3,g1)
    c: Coincident(g4,g1)
    c: Coincident(g4,g-1)
    c: Angle(g-2,g4) = 0.628319
    c: Coincident(g5,g6)
    c: Coincident(g6,g7)
    c: Coincident(g7,g8)
    c: Horizontal(g8)
    c: Coincident(g8,g9)
    c: Coincident(g5,g9)
    c: Vertical(g7)
    c: Vertical(g9)
    c: Symmetric(g5,g6,g-2)
    c: Tangent(g5,g0)
    c: Tangent(g6,g0)
    c: DistanceX(g8,g8) = 6
    c: Angle(g5,g6) = 1.74533
    c: DistanceY(g7,g7) = 3.5
FEATURE [Sketcher::SketchObject] Sketch022
  Placement = pos=(0,0,100) rot=(0.57735,0.57735,0.57735;2.0944rad)
  sketch-geometry (13):
    g0: LineSegment [constr] StartX=-2.5 StartY=6.31119 StartZ=0 EndX=0 EndY=4.21345 EndZ=0
    g1: LineSegment StartX=0 StartY=4.21345 StartZ=0 EndX=2.5 EndY=6.31119 EndZ=0
    g2: LineSegment StartX=2.5 StartY=6.31119 StartZ=0 EndX=2.5 EndY=0 EndZ=0
    g3: LineSegment [constr] StartX=-2.5 StartY=0 StartZ=0 EndX=-2.5 EndY=6.31119 EndZ=0
    g4: LineSegment [constr] StartX=-2.5 StartY=6.31119 StartZ=0 EndX=2.5 EndY=6.31119 EndZ=0
    g5: Circle [constr] CenterX=-1e-12 CenterY=7.28115 CenterZ=0 NormalX=0 NormalY=0 NormalZ=1 Radius=2.35
    g6: LineSegment [constr] StartX=-2.5 StartY=0 StartZ=0 EndX=2.5 EndY=0 EndZ=0
    g7: Circle [constr] CenterX=-4.27975 CenterY=5.89058 CenterZ=0 NormalX=0 NormalY=0 NormalZ=1 Radius=2.25
    g8: Circle [constr] CenterX=-1e-12 CenterY=7.28115 CenterZ=0 NormalX=0 NormalY=0 NormalZ=1 Radius=2.25
    g9: ArcOfCircle [constr] CenterX=0 CenterY=0 CenterZ=0 NormalX=0 NormalY=0 NormalZ=1 Radius=7.28115 StartAngle=1.5708 EndAngle=2.19911
    g10: LineSegment [constr] StartX=-4.27975 StartY=5.89058 StartZ=0 EndX=0 EndY=0 EndZ=0
    g11: LineSegment StartX=0 StartY=4.21345 StartZ=0 EndX=0 EndY=0 EndZ=0
    g12: LineSegment StartX=0 StartY=0 StartZ=0 EndX=2.5 EndY=0 EndZ=0
  constraints (33):
    c: PointOnObject(g0,g-2)
    c: Coincident(g0,g1)
    c: Coincident(g1,g2)
    c: Coincident(g3,g0)
    c: Vertical(g3)
    c: Coincident(g4,g0)
    c: Coincident(g4,g1)
    c: Horizontal(g4)
    c: PointOnObject(g5,g-2)
    c: Tangent(g1,g5)
    c: Radius(g5) = 2.35
    c: Tangent(g5,g0)
    c: Angle(g1,g0) = 1.74533
    c: DistanceX(g4,g4) = 5
    c: Vertical(g2)
    c: Coincident(g6,g3)
    c: Coincident(g6,g2)
    c: PointOnObject(g3,g-1)
    c: PointOnObject(g2,g-1)
    c: Coincident(g8,g5)
    c: Radius(g8) = 2.25
    c: Equal(g8,g7)
    c: Tangent(g7,g8)
    c: Coincident(g9,g-1)
    c: Coincident(g9,g5)
    c: Coincident(g9,g7)
    c: Coincident(g10,g7)
    c: Coincident(g10,g-1)
    c: Angle(g-2,g10) = 0.628319
    c: Coincident(g0,g11)
    c: Coincident(g11,g12)
    c: Coincident(g12,g2)
    c: Coincident(g11,g-1)
FEATURE [PartDesign::Revolution] Revolution004
  Angle = 360
  Axis = (0,1,0)
  Base = (0,0,100)
  Placement = pos=(0,0,100) rot=(0.57735,0.57735,0.57735;2.0944rad)
  ReferenceAxis = -> Sketch022 [H_Axis]
  Sketch = -> Sketch022
FEATURE [Sketcher::SketchObject] Sketch023
  Placement = pos=(0,0,0) rot=(-1,0,0;4.71239rad)
FEATURE [PartDesign::Revolution] Revolution005
  Angle = 360
  Axis = (0,1,0)
  Base = (0,0,100)
  Placement = pos=(0,0,100) rot=(0.57735,0.57735,0.57735;2.0944rad)
  ReferenceAxis = -> Sketch021 [H_Axis]
  Sketch = -> Sketch021
FEATURE [Sketcher::SketchObject] Sketch024
  Placement = pos=(0,0,0) rot=(-1,0,0;4.71239rad)
  sketch-geometry (8):
    g0: ArcOfCircle CenterX=0 CenterY=100 CenterZ=0 NormalX=0 NormalY=0 NormalZ=1 Radius=12 StartAngle=0.223556 EndAngle=2.91804
    g1: LineSegment StartX=11.7014 StartY=102.66 StartZ=0 EndX=9.34724 EndY=198.303 EndZ=0
    g2: LineSegment StartX=-9.49989 StartY=200.046 StartZ=0 EndX=-11.7014 EndY=102.66 EndZ=0
    g3: ArcOfCircle CenterX=0 CenterY=200 CenterZ=0 NormalX=0 NormalY=0 NormalZ=1 Radius=9.5 StartAngle=3.13671 EndAngle=6.10361
    g4: LineSegment [constr] StartX=-0.00995835 StartY=221.418 StartZ=0 EndX=-70.0813 EndY=150.074 EndZ=0
    g5: LineSegment [constr] StartX=-70.0813 StartY=150.074 StartZ=0 EndX=1.26302 EndY=80.0024 EndZ=0
    g6: LineSegment [constr] StartX=1.26302 StartY=80.0024 StartZ=0 EndX=71.3343 EndY=151.347 EndZ=0
    g7: LineSegment [constr] StartX=71.3343 StartY=151.347 StartZ=0 EndX=-0.00995835 EndY=221.418 EndZ=0
  constraints (20):
    c: PointOnObject(g0,g-2)
    c: Coincident(g0,g1)
    c: Coincident(g2,g0)
    c: PointOnObject(g3,g-2)
    c: Coincident(g3,g1)
    c: Symmetric(g0,g0,g-2)
    c: Radius(g0) = 12
    c: Coincident(g3,g2)
    c: DistanceY(g-1,g0) = 100
    c: DistanceY(g0,g3) = 100
    c: Coincident(g4,g5)
    c: Coincident(g5,g6)
    c: Coincident(g6,g7)
    c: Coincident(g7,g4)
    c: Equal(g4,g7)
    c: Equal(g7,g5)
    c: Equal(g5,g6)
    c: Perpendicular(g7,g4)
    c: Distance(g7) = 100
    c: Radius(g3) = 9.5
FEATURE [PartDesign::Pad] Pad012
  Length = 3
  Length2 = 100
  Placement = pos=(0,0,0) rot=(-1,0,0;4.71239rad)
  Sketch = -> Sketch024
  Type = 0
FEATURE [Sketcher::SketchObject] Sketch025
  Placement = pos=(0,0,200) rot=(0.57735,0.57735,0.57735;2.0944rad)
  sketch-geometry (10):
    g0: Circle [constr] CenterX=0 CenterY=5.18572 CenterZ=0 NormalX=0 NormalY=0 NormalZ=1 Radius=2.35
    g1: Circle [constr] CenterX=-4.05436 CenterY=3.23324 CenterZ=0 NormalX=0 NormalY=0 NormalZ=1 Radius=2.25
    g2: Circle [constr] CenterX=0 CenterY=5.18572 CenterZ=0 NormalX=0 NormalY=0 NormalZ=1 Radius=2.25
    g3: ArcOfCircle [constr] CenterX=0 CenterY=0 CenterZ=0 NormalX=0 NormalY=0 NormalZ=1 Radius=5.18572 StartAngle=1.5708 EndAngle=2.46839
    g4: LineSegment [constr] StartX=-4.05436 StartY=3.23324 StartZ=0 EndX=0 EndY=0 EndZ=0
    g5: LineSegment StartX=-3 StartY=5.73613 StartZ=0 EndX=0 EndY=8.25343 EndZ=0
    g6: LineSegment StartX=0 StartY=8.25343 StartZ=0 EndX=3 EndY=5.73613 EndZ=0
    g7: LineSegment StartX=3 StartY=5.73613 StartZ=0 EndX=3 EndY=9.23613 EndZ=0
    g8: LineSegment StartX=3 StartY=9.23613 StartZ=0 EndX=-3 EndY=9.23613 EndZ=0
    g9: LineSegment StartX=-3 StartY=9.23613 StartZ=0 EndX=-3 EndY=5.73613 EndZ=0
  constraints (26):
    c: PointOnObject(g0,g-2)
    c: Radius(g0) = 2.35
    c: Coincident(g2,g0)
    c: Radius(g2) = 2.25
    c: Equal(g2,g1)
    c: Tangent(g1,g2)
    c: Coincident(g3,g-1)
    c: Coincident(g3,g0)
    c: Coincident(g3,g1)
    c: Coincident(g4,g1)
    c: Coincident(g4,g-1)
    c: Angle(g-2,g4) = 0.897598
    c: Coincident(g5,g6)
    c: Coincident(g6,g7)
    c: Coincident(g7,g8)
    c: Horizontal(g8)
    c: Coincident(g8,g9)
    c: Coincident(g5,g9)
    c: Vertical(g7)
    c: Vertical(g9)
    c: Symmetric(g5,g6,g-2)
    c: Tangent(g5,g0)
    c: Tangent(g6,g0)
    c: DistanceX(g8,g8) = 6
    c: Angle(g5,g6) = 1.74533
    c: DistanceY(g7,g7) = 3.5
FEATURE [PartDesign::Revolution] Revolution006
  Angle = 360
  Axis = (0,1,0)
  Base = (0,0,200)
  Placement = pos=(0,0,200) rot=(0.57735,0.57735,0.57735;2.0944rad)
  ReferenceAxis = -> Sketch025 [H_Axis]
  Sketch = -> Sketch025
